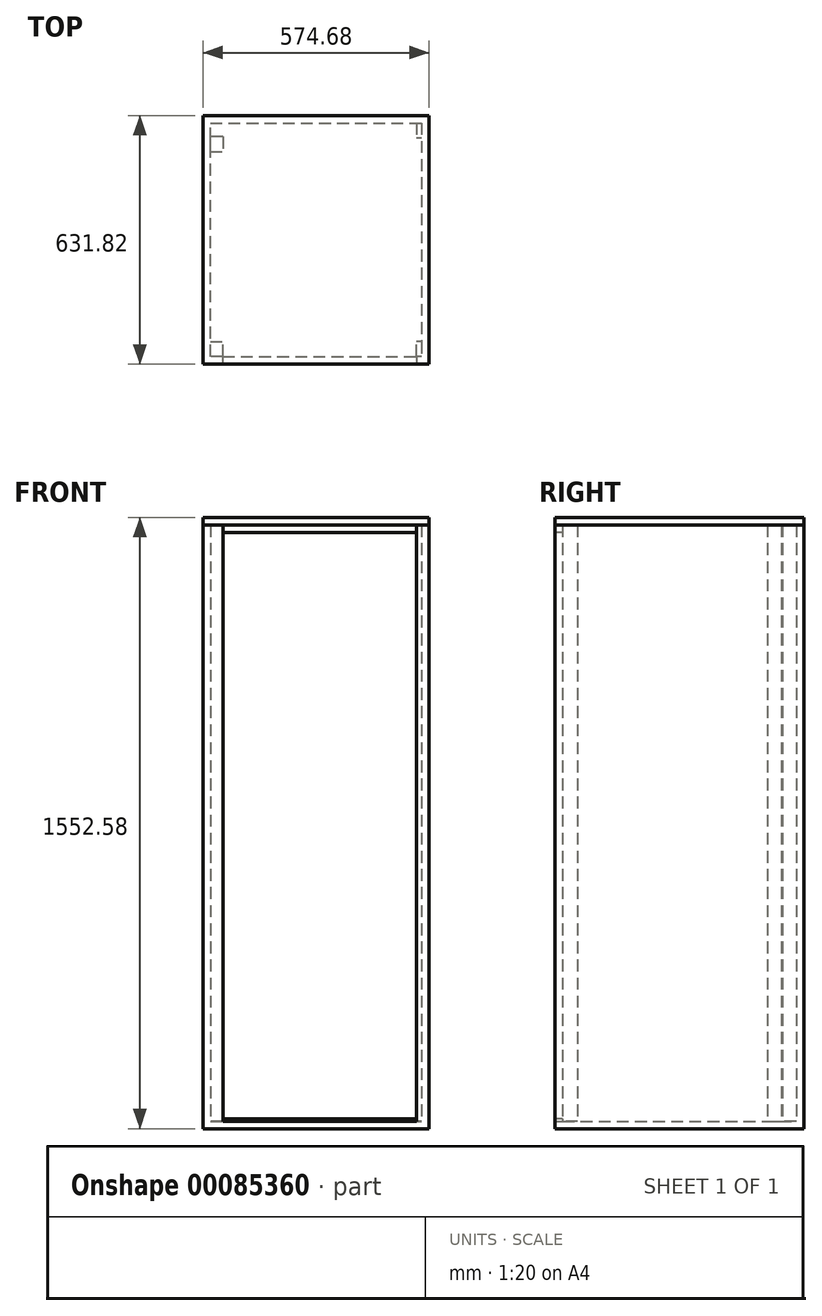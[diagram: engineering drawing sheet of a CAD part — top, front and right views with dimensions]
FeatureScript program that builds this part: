
annotation { "Feature Type Name" : "Feature", "Feature Type Description" : "" }
export const myFeature = defineFeature(function(context is Context, id is Id, definition is map)
    precondition{}
    {
        {
            var Q0;
            Q0=qCreatedBy(makeId("Top.planeOp"),FACE);
            var sketch = newSketch(context, id + "F0", { "sketchPlane" : qUnion([Q0])});
            skLineSegment(sketch, "E0", {"start": v(0, 0) * mm, "end": v(50.8, 0) * mm});
            skLineSegment(sketch, "E1", {"start": v(50.8, 0) * mm, "end": v(50.8, 19.05) * mm});
            skLineSegment(sketch, "E2", {"start": v(50.8, 19.05) * mm, "end": v(19.05, 19.05) * mm});
            skLineSegment(sketch, "E3", {"start": v(19.05, 19.05) * mm, "end": v(19.05, 612.78) * mm});
            skLineSegment(sketch, "E4", {"start": v(19.05, 612.78) * mm, "end": v(555.62, 612.78) * mm});
            skLineSegment(sketch, "E5", {"start": v(555.62, 612.78) * mm, "end": v(555.62, 19.05) * mm});
            skLineSegment(sketch, "E6", {"start": v(555.62, 19.05) * mm, "end": v(542.92, 19.05) * mm});
            skLineSegment(sketch, "E7", {"start": v(542.92, 19.05) * mm, "end": v(542.92, 0) * mm});
            skLineSegment(sketch, "E8", {"start": v(542.92, 0) * mm, "end": v(574.68, 0) * mm});
            skLineSegment(sketch, "E9", {"start": v(574.68, 0) * mm, "end": v(574.68, 631.83) * mm});
            skLineSegment(sketch, "E10", {"start": v(574.68, 631.83) * mm, "end": v(0, 631.83) * mm});
            skLineSegment(sketch, "E11", {"start": v(0, 631.83) * mm, "end": v(0, 0) * mm});
            skSolve(sketch);
        }
        {
            var Q0;
            Q0=makeQuery(id+"F0.imprint","IMPRINT",FACE,{"disambiguationData":[TD([[makeQuery(id+"F0.imprint","IMPRINT",EDGE,{"derivedFrom":sQuery(id+"F0.wireOp",EDGE,"E0")}),1.0]])]});
            extrude(context, id + "F1", {"entities" : qUnion([Q0]), "depth" : 1514.47 * mm});
        }
        {
            var Q0;
            Q0=makeQuery(id+"F1.opExtrude","CAP_FACE",FACE,{"disambiguationData":[OSD([sQuery(id+"F0.wireOp",EDGE,"E0"),sQuery(id+"F0.wireOp",EDGE,"E1"),sQuery(id+"F0.wireOp",EDGE,"E2"),sQuery(id+"F0.wireOp",EDGE,"E3"),sQuery(id+"F0.wireOp",EDGE,"E4"),sQuery(id+"F0.wireOp",EDGE,"E5"),sQuery(id+"F0.wireOp",EDGE,"E6"),sQuery(id+"F0.wireOp",EDGE,"E7"),sQuery(id+"F0.wireOp",EDGE,"E8"),sQuery(id+"F0.wireOp",EDGE,"E9"),sQuery(id+"F0.wireOp",EDGE,"E10"),sQuery(id+"F0.wireOp",EDGE,"E11")])],"isStart":false});
            var sketch = newSketch(context, id + "F2", { "sketchPlane" : qUnion([Q0])});
            skLineSegment(sketch, "E12.bottom", {"start": v(0, 631.83) * mm, "end": v(574.68, 631.83) * mm});
            skLineSegment(sketch, "E12.top", {"start": v(0, 0) * mm, "end": v(574.68, 0) * mm});
            skLineSegment(sketch, "E12.left", {"start": v(0, 631.83) * mm, "end": v(0, 0) * mm});
            skLineSegment(sketch, "E12.right", {"start": v(574.68, 631.83) * mm, "end": v(574.68, 0) * mm});
            skSolve(sketch);
        }
        {
            var Q0;
            Q0=makeQuery(id+"F2.imprint","IMPRINT",FACE,{"disambiguationData":[TD([[makeQuery(id+"F2.imprint","IMPRINT",EDGE,{"derivedFrom":sQuery(id+"F2.wireOp",EDGE,"E12.bottom")}),1.0]])]});
            var Q1;
            {var subQ0=makeQuery(id+"F1.opExtrude","CAP_EDGE",EDGE,{"disambiguationData":[OSD([sQuery(id+"F0.wireOp",EDGE,"E1")])],"isStart":false});Q1=makeQuery(id+"F2.imprint","IMPRINT",FACE,{"disambiguationData":[TD([[makeQuery(id+"F2.imprint","IMPRINT",EDGE,{"derivedFrom":subQ0}),-1.0]])]});}
            extrude(context, id + "F3", {"entities" : qUnion([Q0, Q1]), "depth" : 19.05 * mm});
        }
        {
            var Q0;
            Q0=makeQuery(id+"F1.opExtrude","CAP_FACE",FACE,{"disambiguationData":[OSD([sQuery(id+"F0.wireOp",EDGE,"E0"),sQuery(id+"F0.wireOp",EDGE,"E1"),sQuery(id+"F0.wireOp",EDGE,"E2"),sQuery(id+"F0.wireOp",EDGE,"E3"),sQuery(id+"F0.wireOp",EDGE,"E4"),sQuery(id+"F0.wireOp",EDGE,"E5"),sQuery(id+"F0.wireOp",EDGE,"E6"),sQuery(id+"F0.wireOp",EDGE,"E7"),sQuery(id+"F0.wireOp",EDGE,"E8"),sQuery(id+"F0.wireOp",EDGE,"E9"),sQuery(id+"F0.wireOp",EDGE,"E10"),sQuery(id+"F0.wireOp",EDGE,"E11")])],"isStart":true});
            var sketch = newSketch(context, id + "F4", { "sketchPlane" : qUnion([Q0])});
            skLineSegment(sketch, "E13.bottom", {"start": v(0, 0) * mm, "end": v(574.68, 0) * mm});
            skLineSegment(sketch, "E13.top", {"start": v(0, -631.83) * mm, "end": v(574.68, -631.83) * mm});
            skLineSegment(sketch, "E13.left", {"start": v(0, 0) * mm, "end": v(0, -631.83) * mm});
            skLineSegment(sketch, "E13.right", {"start": v(574.68, 0) * mm, "end": v(574.68, -631.83) * mm});
            skSolve(sketch);
        }
        {
            var Q0;
            {var subQ0=makeQuery(id+"F1.opExtrude","CAP_EDGE",EDGE,{"disambiguationData":[OSD([sQuery(id+"F0.wireOp",EDGE,"E1")])],"isStart":true});Q0=makeQuery(id+"F4.imprint","IMPRINT",FACE,{"disambiguationData":[TD([[makeQuery(id+"F4.imprint","IMPRINT",EDGE,{"derivedFrom":subQ0}),1.0]])]});}
            var Q1;
            Q1=makeQuery(id+"F4.imprint","IMPRINT",FACE,{"disambiguationData":[TD([[makeQuery(id+"F4.imprint","IMPRINT",EDGE,{"derivedFrom":sQuery(id+"F4.wireOp",EDGE,"E13.top")}),-1.0]])]});
            extrude(context, id + "F5", {"entities" : qUnion([Q0, Q1]), "operationType" : NewBodyOperationType.ADD, "depth" : 19.05 * mm});
        }
        {
            var Q0;
            Q0=makeQuery(id+"F5.boolean.opBoolean","MERGE",FACE,{"derivedFrom":[makeQuery(id+"F1.opExtrude","SWEPT_FACE",FACE,{"disambiguationData":[OSD([sQuery(id+"F0.wireOp",EDGE,"E0")])]}),makeQuery(id+"F1.opExtrude","SWEPT_FACE",FACE,{"disambiguationData":[OSD([sQuery(id+"F0.wireOp",EDGE,"E8")])]}),makeQuery(id+"F5.opExtrude","SWEPT_FACE",FACE,{"disambiguationData":[OSD([sQuery(id+"F4.wireOp",EDGE,"E13.bottom")])]})]});
            var sketch = newSketch(context, id + "F6", { "sketchPlane" : qUnion([Q0])});
            skLineSegment(sketch, "E14.bottom", {"start": v(50.8, 0) * mm, "end": v(542.92, 0) * mm});
            skLineSegment(sketch, "E14.top", {"start": v(50.8, 6.35) * mm, "end": v(542.92, 6.35) * mm});
            skLineSegment(sketch, "E14.left", {"start": v(50.8, 0) * mm, "end": v(50.8, 6.35) * mm});
            skLineSegment(sketch, "E14.right", {"start": v(542.92, 0) * mm, "end": v(542.92, 6.35) * mm});
            skSolve(sketch);
        }
        {
            var Q0;
            Q0=makeQuery(id+"F6.imprint","IMPRINT",FACE,{"disambiguationData":[TD([[makeQuery(id+"F6.imprint","IMPRINT",EDGE,{"derivedFrom":sQuery(id+"F6.wireOp",EDGE,"E14.bottom")}),1.0]])]});
            extrude(context, id + "F7", {"entities" : qUnion([Q0]), "oppositeDirection" : true, "depth" : 19.05 * mm});
        }
        {
            var Q0;
            Q0=makeQuery(id+"F7.boolean.opBoolean","MERGE",FACE,{"derivedFrom":[makeQuery(id+"F5.boolean.opBoolean","MERGE",FACE,{"derivedFrom":[makeQuery(id+"F1.opExtrude","SWEPT_FACE",FACE,{"disambiguationData":[OSD([sQuery(id+"F0.wireOp",EDGE,"E0")])]}),makeQuery(id+"F1.opExtrude","SWEPT_FACE",FACE,{"disambiguationData":[OSD([sQuery(id+"F0.wireOp",EDGE,"E8")])]}),makeQuery(id+"F5.opExtrude","SWEPT_FACE",FACE,{"disambiguationData":[OSD([sQuery(id+"F4.wireOp",EDGE,"E13.bottom")])]})]}),makeQuery(id+"F7.opExtrude","CAP_FACE",FACE,{"disambiguationData":[OSD([sQuery(id+"F6.wireOp",EDGE,"E14.bottom"),sQuery(id+"F6.wireOp",EDGE,"E14.top"),sQuery(id+"F6.wireOp",EDGE,"E14.left"),sQuery(id+"F6.wireOp",EDGE,"E14.right")])],"isStart":true})]});
            var sketch = newSketch(context, id + "F8", { "sketchPlane" : qUnion([Q0])});
            skLineSegment(sketch, "E15.bottom", {"start": v(50.8, 1514.48) * mm, "end": v(542.92, 1514.48) * mm});
            skLineSegment(sketch, "E15.top", {"start": v(50.8, 1495.43) * mm, "end": v(542.92, 1495.43) * mm});
            skLineSegment(sketch, "E15.left", {"start": v(50.8, 1514.48) * mm, "end": v(50.8, 1495.43) * mm});
            skLineSegment(sketch, "E15.right", {"start": v(542.92, 1514.48) * mm, "end": v(542.92, 1495.43) * mm});
            skSolve(sketch);
        }
        {
            var Q0;
            Q0=makeQuery(id+"F8.imprint","IMPRINT",FACE,{"disambiguationData":[TD([[makeQuery(id+"F8.imprint","IMPRINT",EDGE,{"derivedFrom":sQuery(id+"F8.wireOp",EDGE,"E15.bottom")}),-1.0]])]});
            extrude(context, id + "F9", {"entities" : qUnion([Q0]), "oppositeDirection" : true, "depth" : 19.05 * mm});
        }
        {
            var Q0;
            Q0=makeQuery(id+"F5.opExtrude","CAP_FACE",FACE,{"disambiguationData":[OSD([sQuery(id+"F4.wireOp",EDGE,"E13.bottom"),sQuery(id+"F4.wireOp",EDGE,"E13.top"),sQuery(id+"F4.wireOp",EDGE,"E13.left"),sQuery(id+"F4.wireOp",EDGE,"E13.right")])],"isStart":true});
            var sketch = newSketch(context, id + "F10", { "sketchPlane" : qUnion([Q0])});
            skLineSegment(sketch, "E16.top", {"start": v(19.05, 539.75) * mm, "end": v(50.8, 539.75) * mm});
            skLineSegment(sketch, "E16.left", {"start": v(19.05, 577.85) * mm, "end": v(19.05, 539.75) * mm});
            skLineSegment(sketch, "E16.right", {"start": v(50.8, 577.85) * mm, "end": v(50.8, 539.75) * mm});
            skLineSegment(sketch, "E17.bottom", {"start": v(19.05, 19.05) * mm, "end": v(50.8, 19.05) * mm});
            skLineSegment(sketch, "E17.top", {"start": v(19.05, 57.15) * mm, "end": v(50.8, 57.15) * mm});
            skLineSegment(sketch, "E17.left", {"start": v(19.05, 19.05) * mm, "end": v(19.05, 57.15) * mm});
            skLineSegment(sketch, "E17.right", {"start": v(50.8, 19.05) * mm, "end": v(50.8, 57.15) * mm});
            skLineSegment(sketch, "E18.bottom", {"start": v(555.62, 612.78) * mm, "end": v(542.92, 612.78) * mm});
            skLineSegment(sketch, "E18.top", {"start": v(555.62, 574.68) * mm, "end": v(542.92, 574.68) * mm});
            skLineSegment(sketch, "E18.left", {"start": v(555.62, 612.78) * mm, "end": v(555.62, 574.68) * mm});
            skLineSegment(sketch, "E18.right", {"start": v(542.92, 612.78) * mm, "end": v(542.92, 574.68) * mm});
            skLineSegment(sketch, "E19.bottom", {"start": v(555.62, 19.05) * mm, "end": v(542.92, 19.05) * mm});
            skLineSegment(sketch, "E19.top", {"start": v(555.62, 57.15) * mm, "end": v(542.92, 57.15) * mm});
            skLineSegment(sketch, "E19.left", {"start": v(555.62, 19.05) * mm, "end": v(555.62, 57.15) * mm});
            skLineSegment(sketch, "E19.right", {"start": v(542.92, 19.05) * mm, "end": v(542.92, 57.15) * mm});
            skLineSegment(sketch, "E20", {"start": v(50.8, 577.85) * mm, "end": v(19.05, 577.85) * mm});
            skSolve(sketch);
        }
        {
            var Q0;
            Q0=makeQuery(id+"F10.imprint","IMPRINT",FACE,{"disambiguationData":[TD([[makeQuery(id+"F10.imprint","IMPRINT",EDGE,{"derivedFrom":sQuery(id+"F10.wireOp",EDGE,"E16.bottom")}),-1.0]])]});
            var Q1;
            Q1=makeQuery(id+"F10.imprint","IMPRINT",FACE,{"disambiguationData":[TD([[makeQuery(id+"F10.imprint","IMPRINT",EDGE,{"derivedFrom":sQuery(id+"F10.wireOp",EDGE,"E18.bottom")}),-1.0]])]});
            var Q2;
            Q2=makeQuery(id+"F10.imprint","IMPRINT",FACE,{"disambiguationData":[TD([[makeQuery(id+"F10.imprint","IMPRINT",EDGE,{"derivedFrom":sQuery(id+"F10.wireOp",EDGE,"E19.bottom")}),-1.0]])]});
            var Q3;
            Q3=makeQuery(id+"F10.imprint","IMPRINT",FACE,{"disambiguationData":[TD([[makeQuery(id+"F10.imprint","IMPRINT",EDGE,{"derivedFrom":sQuery(id+"F10.wireOp",EDGE,"E17.bottom")}),-1.0]])]});
            var Q4;
            Q4=makeQuery(id+"F10.imprint","IMPRINT",FACE,{"disambiguationData":[TD([[makeQuery(id+"F10.imprint","IMPRINT",EDGE,{"derivedFrom":sQuery(id+"F10.wireOp",EDGE,"E16.top")}),1.0]])]});
            extrude(context, id + "F11", {"entities" : qUnion([Q0, Q1, Q2, Q3, Q4]), "endBound" : BoundingType.UP_TO_NEXT, "depth" : 25.4 * mm});
        }
        {
            var Q0;
            Q0=makeQuery(id+"F1.opExtrude","SWEPT_FACE",FACE,{"disambiguationData":[OSD([sQuery(id+"F0.wireOp",EDGE,"E4")])]});
            var sketch = newSketch(context, id + "F12", { "sketchPlane" : qUnion([Q0])});
            skLineSegment(sketch, "E21", {"start": v(296.86, 0) * mm, "end": v(296.86, 1514.48) * mm});
            skPoint(sketch, "E22", {"position": v(296.86, 34.93) * mm});
            skPoint(sketch, "E23", {"position": v(296.86, 285.75) * mm});
            skPoint(sketch, "E24", {"position": v(296.86, 539.75) * mm});
            skPoint(sketch, "E25", {"position": v(296.86, 742.95) * mm});
            skPoint(sketch, "E26", {"position": v(296.86, 946.15) * mm});
            skPoint(sketch, "E27", {"position": v(296.86, 1149.35) * mm});
            skPoint(sketch, "E28", {"position": v(296.86, 0) * mm});
            skSolve(sketch);
        }
        {
            var Q0;
            Q0=makeQuery(id+"F1.opExtrude","SWEPT_FACE",FACE,{"disambiguationData":[OSD([sQuery(id+"F0.wireOp",EDGE,"E7")])]});
            var sketch = newSketch(context, id + "F13", { "sketchPlane" : qUnion([Q0])});
            skPoint(sketch, "E29", {"position": v(-19.05, 57.15) * mm});
            skPoint(sketch, "E30", {"position": v(-19.05, 387.35) * mm});
            skPoint(sketch, "E31", {"position": v(-19.05, 666.75) * mm});
            skPoint(sketch, "E32", {"position": v(-19.05, 895.35) * mm});
            skPoint(sketch, "E33", {"position": v(-19.05, 1098.55) * mm});
            skPoint(sketch, "E34", {"position": v(-19.05, 1289.56) * mm});
            skSolve(sketch);
        }
    });
